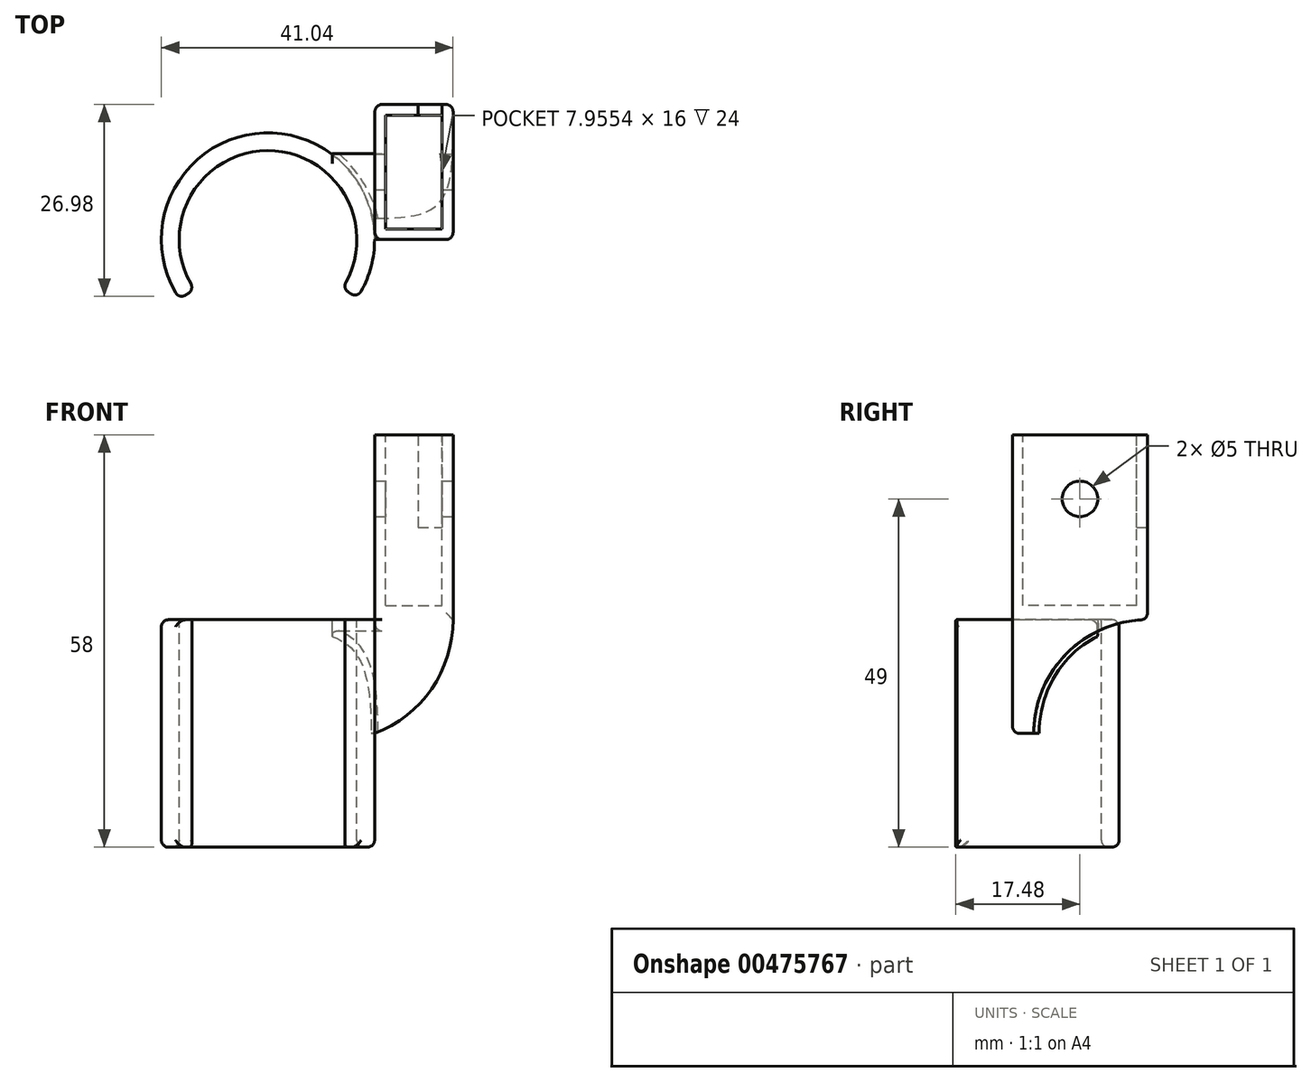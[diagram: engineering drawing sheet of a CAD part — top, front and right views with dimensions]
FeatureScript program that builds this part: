
annotation { "Feature Type Name" : "Feature", "Feature Type Description" : "" }
export const myFeature = defineFeature(function(context is Context, id is Id, definition is map)
    precondition{}
    {
        {
            var Q0;
            Q0=qCreatedBy(makeId("Top.planeOp"),FACE);
            var sketch = newSketch(context, id + "F0", { "sketchPlane" : qUnion([Q0])});
            skLineSegment(sketch, "E0.bottom", {"start": v(0.04, 0) * mm, "end": v(11.04, 0) * mm});
            skLineSegment(sketch, "E0.top", {"start": v(0.04, 19) * mm, "end": v(11.04, 19) * mm});
            skLineSegment(sketch, "E0.left", {"start": v(0.04, 0) * mm, "end": v(0.04, 19) * mm});
            skLineSegment(sketch, "E0.right", {"start": v(11.04, 0) * mm, "end": v(11.04, 19) * mm});
            skPoint(sketch, "E1", {"position": v(0, -4.92) * mm});
            skPoint(sketch, "E2", {"position": v(0.04, 0) * mm});
            skSolve(sketch);
        }
        {
            var Q0;
            Q0 = qSketchRegion(id + "F0", true);
            extrude(context, id + "F1", {"entities" : qUnion([Q0]), "depth" : 26 * mm, "hasSecondDirection" : true, "secondDirectionOppositeDirection" : true, "secondDirectionDepth" : 16 * mm});
        }
        {
            var Q0;
            Q0=makeQuery(id+"F1.opExtrude","SWEPT_FACE",FACE,{"disambiguationData":[OSD([sQuery(id+"F0.wireOp",EDGE,"E0.left")])]});
            var sketch = newSketch(context, id + "F2", { "sketchPlane" : qUnion([Q0])});
            skLineSegment(sketch, "E3.bottom", {"start": v(0, 0) * mm, "end": v(-19, 0) * mm});
            skLineSegment(sketch, "E3.top", {"start": v(0, -16) * mm, "end": v(-19, -16) * mm});
            skLineSegment(sketch, "E3.left", {"start": v(0, 0) * mm, "end": v(0, -16) * mm});
            skLineSegment(sketch, "E3.right", {"start": v(-19, 0) * mm, "end": v(-19, -16) * mm});
            skSolve(sketch);
        }
        {
            var Q0;
            Q0 = qSketchRegion(id + "F2", true);
            extrude(context, id + "F3", {"entities" : qUnion([Q0]), "operationType" : NewBodyOperationType.ADD, "depth" : 6 * mm});
        }
        {
            var Q0;
            Q0=makeQuery(id+"F1.opExtrude","SWEPT_FACE",FACE,{"disambiguationData":[OSD([sQuery(id+"F0.wireOp",EDGE,"E0.right")])]});
            var sketch = newSketch(context, id + "F4", { "sketchPlane" : qUnion([Q0])});
            skCircle(sketch, "E4", {"center": v(19, -16) * mm, "radius": 16 * mm});
            skSolve(sketch);
        }
        {
            var Q0;
            Q0 = qSketchRegion(id + "F4", true);
            extrude(context, id + "F5", {"entities" : qUnion([Q0]), "operationType" : NewBodyOperationType.REMOVE, "oppositeDirection" : true, "depth" : 25 * mm});
        }
        {
            var Q0;
            Q0=makeQuery(id+"F3.boolean.opBoolean","MERGE",FACE,{"derivedFrom":[makeQuery(id+"F1.opExtrude","SWEPT_FACE",FACE,{"disambiguationData":[OSD([sQuery(id+"F0.wireOp",EDGE,"E0.bottom")])]}),makeQuery(id+"F3.opExtrude","SWEPT_FACE",FACE,{"disambiguationData":[OSD([sQuery(id+"F2.wireOp",EDGE,"E3.left")])]})]});
            var sketch = newSketch(context, id + "F6", { "sketchPlane" : qUnion([Q0])});
            skLineSegment(sketch, "E5", {"start": v(0, -16) * mm, "end": v(11.04, -16) * mm});
            skLineSegment(sketch, "E6", {"start": v(11.04, -16) * mm, "end": v(11.04, 0) * mm});
            skArc(sketch, "E7", {"start": v(0, -16) * mm, "mid": v(8.02, -9.72) * mm, "end": v(11.04, 0) * mm});
            skSolve(sketch);
        }
        {
            var Q0;
            Q0 = qSketchRegion(id + "F6", true);
            extrude(context, id + "F7", {"entities" : qUnion([Q0]), "operationType" : NewBodyOperationType.REMOVE, "oppositeDirection" : true, "depth" : 25 * mm});
        }
        {
            var Q0;
            Q0=qCreatedBy(makeId("Top.planeOp"),FACE);
            var sketch = newSketch(context, id + "F8", { "sketchPlane" : qUnion([Q0])});
            skCircle(sketch, "E8", {"center": v(-15, 0) * mm, "radius": 15 * mm});
            skSolve(sketch);
        }
        {
            var Q0;
            Q0 = qSketchRegion(id + "F8", true);
            extrude(context, id + "F9", {"entities" : qUnion([Q0]), "operationType" : NewBodyOperationType.ADD, "oppositeDirection" : true, "depth" : 32 * mm});
        }
        {
            var Q0;
            Q0=makeQuery(id+"F9.boolean.opBoolean","MERGE",FACE,{"derivedFrom":[makeQuery(id+"F3.opExtrude","SWEPT_FACE",FACE,{"disambiguationData":[OSD([sQuery(id+"F2.wireOp",EDGE,"E3.bottom")])]}),makeQuery(id+"F9.opExtrude","CAP_FACE",FACE,{"disambiguationData":[OSD([sQuery(id+"F8.wireOp",EDGE,"E8")])],"isStart":true})]});
            var sketch = newSketch(context, id + "F10", { "sketchPlane" : qUnion([Q0])});
            skLineSegment(sketch, "E9.bottom", {"start": v(-5.96, 19) * mm, "end": v(0.04, 19) * mm});
            skLineSegment(sketch, "E9.top", {"start": v(-5.96, 12.05) * mm, "end": v(0.04, 12.05) * mm});
            skLineSegment(sketch, "E9.left", {"start": v(-5.96, 19) * mm, "end": v(-5.96, 12.05) * mm});
            skLineSegment(sketch, "E9.right", {"start": v(0.04, 19) * mm, "end": v(0.04, 12.05) * mm});
            skSolve(sketch);
        }
        {
            var Q0;
            Q0 = qSketchRegion(id + "F10", true);
            extrude(context, id + "F11", {"entities" : qUnion([Q0]), "operationType" : NewBodyOperationType.REMOVE, "oppositeDirection" : true, "depth" : 25 * mm});
        }
        {
            var Q0;
            Q0=makeQuery(id+"F9.boolean.opBoolean","MERGE",FACE,{"derivedFrom":[makeQuery(id+"F3.opExtrude","SWEPT_FACE",FACE,{"disambiguationData":[OSD([sQuery(id+"F2.wireOp",EDGE,"E3.bottom")])]}),makeQuery(id+"F9.opExtrude","CAP_FACE",FACE,{"disambiguationData":[OSD([sQuery(id+"F8.wireOp",EDGE,"E8")])],"isStart":true})]});
            var sketch = newSketch(context, id + "F12", { "sketchPlane" : qUnion([Q0])});
            skCircle(sketch, "E10", {"center": v(-15, 0) * mm, "radius": 12.5 * mm});
            skSolve(sketch);
        }
        {
            var Q0;
            Q0 = qSketchRegion(id + "F12", true);
            extrude(context, id + "F13", {"entities" : qUnion([Q0]), "operationType" : NewBodyOperationType.REMOVE, "endBound" : BoundingType.THROUGH_ALL, "oppositeDirection" : true, "depth" : 25 * mm});
        }
        {
            var Q0;
            Q0=qCreatedBy(makeId("Top.planeOp"),FACE);
            var sketch = newSketch(context, id + "F14", { "sketchPlane" : qUnion([Q0])});
            skLineSegment(sketch, "E11", {"start": v(6.11, -8) * mm, "end": v(-27.7, -8) * mm, "construction": true});
            skLineSegment(sketch, "E12", {"start": v(-14.82, 0) * mm, "end": v(12.37, -18.05) * mm});
            skLineSegment(sketch, "E13", {"start": v(12.37, -18.05) * mm, "end": v(-42, -18.05) * mm});
            skLineSegment(sketch, "E14", {"start": v(-42, -18.05) * mm, "end": v(-14.82, 0) * mm});
            skSolve(sketch);
        }
        {
            var Q0;
            Q0 = qSketchRegion(id + "F14", true);
            extrude(context, id + "F15", {"entities" : qUnion([Q0]), "operationType" : NewBodyOperationType.REMOVE, "endBound" : BoundingType.THROUGH_ALL, "oppositeDirection" : true, "depth" : 25 * mm});
        }
        {
            var Q0;
            Q0=makeQuery(id+"F9.boolean.opBoolean","INTERSECT",EDGE,{"derivedFrom":[makeQuery(id+"F5.boolean.opBoolean","COPY",FACE,{"derivedFrom":makeQuery(id+"F5.opExtrude","SWEPT_FACE",FACE,{"disambiguationData":[OSD([sQuery(id+"F4.wireOp",EDGE,"E4")])]})}),makeQuery(id+"F9.opExtrude","SWEPT_FACE",FACE,{"disambiguationData":[OSD([sQuery(id+"F8.wireOp",EDGE,"E8")])]})]});
            var Q1;
            Q1=makeQuery(id+"F5.boolean.opBoolean","INTERSECT",EDGE,{"derivedFrom":[makeQuery(id+"F3.boolean.opBoolean","MERGE",FACE,{"derivedFrom":[makeQuery(id+"F1.opExtrude","SWEPT_FACE",FACE,{"disambiguationData":[OSD([sQuery(id+"F0.wireOp",EDGE,"E0.top")])]}),makeQuery(id+"F3.opExtrude","SWEPT_FACE",FACE,{"disambiguationData":[OSD([sQuery(id+"F2.wireOp",EDGE,"E3.right")])]})]}),makeQuery(id+"F5.opExtrude","SWEPT_FACE",FACE,{"disambiguationData":[OSD([sQuery(id+"F4.wireOp",EDGE,"E4")])]})]});
            var Q2;
            Q2=makeQuery(id+"F11.boolean.opBoolean","INTERSECT",EDGE,{"derivedFrom":[makeQuery(id+"F5.boolean.opBoolean","COPY",FACE,{"derivedFrom":makeQuery(id+"F5.opExtrude","SWEPT_FACE",FACE,{"disambiguationData":[OSD([sQuery(id+"F4.wireOp",EDGE,"E4")])]})}),makeQuery(id+"F11.opExtrude","SWEPT_FACE",FACE,{"disambiguationData":[OSD([sQuery(id+"F10.wireOp",EDGE,"E9.right")])]})]});
            var Q3;
            Q3=makeQuery(id+"F1.opExtrude","SWEPT_EDGE",EDGE,{"disambiguationData":[OSD([sQuery(id+"F0.wireOp",EDGE,"E0.top"),sQuery(id+"F0.wireOp",EDGE,"E0.left")])]});
            var Q4;
            Q4=makeQuery(id+"F1.opExtrude","SWEPT_EDGE",EDGE,{"disambiguationData":[OSD([sQuery(id+"F0.wireOp",EDGE,"E0.top"),sQuery(id+"F0.wireOp",EDGE,"E0.right")])]});
            var Q5;
            Q5=makeQuery(id+"F1.opExtrude","SWEPT_EDGE",EDGE,{"disambiguationData":[OSD([sQuery(id+"F0.wireOp",EDGE,"E0.bottom"),sQuery(id+"F0.wireOp",EDGE,"E0.right")])]});
            var Q6;
            Q6=makeQuery(id+"F9.opExtrude","CAP_EDGE",EDGE,{"disambiguationData":[OSD([sQuery(id+"F8.wireOp",EDGE,"E8")])],"isStart":false});
            var Q7;
            Q7=makeQuery(id+"F13.boolean.opBoolean","INTERSECT",EDGE,{"derivedFrom":[makeQuery(id+"F9.opExtrude","CAP_FACE",FACE,{"disambiguationData":[OSD([sQuery(id+"F8.wireOp",EDGE,"E8")])],"isStart":false}),makeQuery(id+"F13.opExtrude","SWEPT_FACE",FACE,{"disambiguationData":[OSD([sQuery(id+"F12.wireOp",EDGE,"E10")])]})]});
            var Q8;
            Q8=makeQuery(id+"F15.boolean.opBoolean","INTERSECT",EDGE,{"derivedFrom":[makeQuery(id+"F13.boolean.opBoolean","COPY",FACE,{"derivedFrom":makeQuery(id+"F13.opExtrude","SWEPT_FACE",FACE,{"disambiguationData":[OSD([sQuery(id+"F12.wireOp",EDGE,"E10")])]})}),makeQuery(id+"F15.opExtrude","SWEPT_FACE",FACE,{"disambiguationData":[OSD([sQuery(id+"F14.wireOp",EDGE,"E12")])]})]});
            var Q9;
            Q9=makeQuery(id+"F15.boolean.opBoolean","INTERSECT",EDGE,{"derivedFrom":[makeQuery(id+"F9.opExtrude","SWEPT_FACE",FACE,{"disambiguationData":[OSD([sQuery(id+"F8.wireOp",EDGE,"E8")])]}),makeQuery(id+"F15.opExtrude","SWEPT_FACE",FACE,{"disambiguationData":[OSD([sQuery(id+"F14.wireOp",EDGE,"E12")])]})]});
            var Q10;
            Q10=makeQuery(id+"F15.boolean.opBoolean","INTERSECT",EDGE,{"derivedFrom":[makeQuery(id+"F13.boolean.opBoolean","COPY",FACE,{"derivedFrom":makeQuery(id+"F13.opExtrude","SWEPT_FACE",FACE,{"disambiguationData":[OSD([sQuery(id+"F12.wireOp",EDGE,"E10")])]})}),makeQuery(id+"F15.opExtrude","SWEPT_FACE",FACE,{"disambiguationData":[OSD([sQuery(id+"F14.wireOp",EDGE,"E14")])]})]});
            var Q11;
            Q11=makeQuery(id+"F15.boolean.opBoolean","INTERSECT",EDGE,{"derivedFrom":[makeQuery(id+"F9.opExtrude","SWEPT_FACE",FACE,{"disambiguationData":[OSD([sQuery(id+"F8.wireOp",EDGE,"E8")])]}),makeQuery(id+"F15.opExtrude","SWEPT_FACE",FACE,{"disambiguationData":[OSD([sQuery(id+"F14.wireOp",EDGE,"E14")])]})]});
            var Q12;
            {var subQ0=sQuery(id+"F8.wireOp",EDGE,"E8");Q12=makeQuery(id+"F15.boolean.opBoolean","SPLIT",EDGE,{"disambiguationData":[TD([makeQuery(id+"F15.opExtrude","SWEPT_FACE",FACE,{"disambiguationData":[OSD([sQuery(id+"F14.wireOp",EDGE,"E14")])]})])],"derivedFrom":makeQuery(id+"F9.opExtrude","CAP_EDGE",EDGE,{"disambiguationData":[OSD([subQ0])],"isStart":true})});}
            var Q13;
            Q13=makeQuery(id+"F13.boolean.opBoolean","COPY",EDGE,{"derivedFrom":makeQuery(id+"F13.opExtrude","CAP_EDGE",EDGE,{"disambiguationData":[OSD([sQuery(id+"F12.wireOp",EDGE,"E10")])],"isStart":true})});
            var Q14;
            Q14=makeQuery(id+"F1.opExtrude","SWEPT_EDGE",EDGE,{"disambiguationData":[OSD([sQuery(id+"F0.wireOp",EDGE,"E0.bottom"),sQuery(id+"F0.wireOp",EDGE,"E0.left")])]});
            fillet(context, id + "F16", {"entities" : qUnion([Q0, Q1, Q2, Q3, Q4, Q5, Q6, Q7, Q8, Q9, Q10, Q11, Q12, Q13, Q14]), "radius" : 1 * mm, "tangentPropagation" : true, "allowEdgeOverflow" : false});
        }
        {
            var Q0;
            Q0=makeQuery(id+"F1.opExtrude","CAP_FACE",FACE,{"disambiguationData":[OSD([sQuery(id+"F0.wireOp",EDGE,"E0.bottom"),sQuery(id+"F0.wireOp",EDGE,"E0.top"),sQuery(id+"F0.wireOp",EDGE,"E0.left"),sQuery(id+"F0.wireOp",EDGE,"E0.right")])],"isStart":false});
            var sketch = newSketch(context, id + "F17", { "sketchPlane" : qUnion([Q0])});
            skLineSegment(sketch, "E15.bottom", {"start": v(1.54, 17.5) * mm, "end": v(9.5, 17.5) * mm});
            skLineSegment(sketch, "E15.top", {"start": v(1.54, 1.5) * mm, "end": v(9.5, 1.5) * mm});
            skLineSegment(sketch, "E15.left", {"start": v(1.54, 17.5) * mm, "end": v(1.54, 1.5) * mm});
            skLineSegment(sketch, "E15.right", {"start": v(9.5, 17.5) * mm, "end": v(9.5, 1.5) * mm});
            skSolve(sketch);
        }
        {
            var Q0;
            Q0 = qSketchRegion(id + "F17", true);
            extrude(context, id + "F18", {"entities" : qUnion([Q0]), "operationType" : NewBodyOperationType.REMOVE, "oppositeDirection" : true, "depth" : 24 * mm});
        }
        {
            var Q0;
            Q0=makeQuery(id+"F1.opExtrude","CAP_FACE",FACE,{"disambiguationData":[OSD([sQuery(id+"F0.wireOp",EDGE,"E0.bottom"),sQuery(id+"F0.wireOp",EDGE,"E0.top"),sQuery(id+"F0.wireOp",EDGE,"E0.left"),sQuery(id+"F0.wireOp",EDGE,"E0.right")])],"isStart":false});
            var sketch = newSketch(context, id + "F19", { "sketchPlane" : qUnion([Q0])});
            skLineSegment(sketch, "E16.bottom", {"start": v(9.5, 14.72) * mm, "end": v(6.1, 14.72) * mm});
            skLineSegment(sketch, "E16.top", {"start": v(9.5, 20.72) * mm, "end": v(6.1, 20.72) * mm});
            skLineSegment(sketch, "E16.left", {"start": v(9.5, 14.72) * mm, "end": v(9.5, 20.72) * mm});
            skLineSegment(sketch, "E16.right", {"start": v(6.1, 14.72) * mm, "end": v(6.1, 20.72) * mm});
            skSolve(sketch);
        }
        {
            var Q0;
            Q0 = qSketchRegion(id + "F19", true);
            extrude(context, id + "F20", {"entities" : qUnion([Q0]), "operationType" : NewBodyOperationType.REMOVE, "oppositeDirection" : true, "depth" : 13 * mm});
        }
        {
            var Q0;
            Q0=makeQuery(id+"F1.opExtrude","SWEPT_FACE",FACE,{"disambiguationData":[OSD([sQuery(id+"F0.wireOp",EDGE,"E0.right")])]});
            var sketch = newSketch(context, id + "F21", { "sketchPlane" : qUnion([Q0])});
            skCircle(sketch, "E17", {"center": v(9.5, 17) * mm, "radius": 2.5 * mm});
            skSolve(sketch);
        }
        {
            var Q0;
            Q0 = qSketchRegion(id + "F21", true);
            extrude(context, id + "F22", {"entities" : qUnion([Q0]), "operationType" : NewBodyOperationType.REMOVE, "endBound" : BoundingType.THROUGH_ALL, "oppositeDirection" : true, "depth" : 25 * mm});
        }
    });
